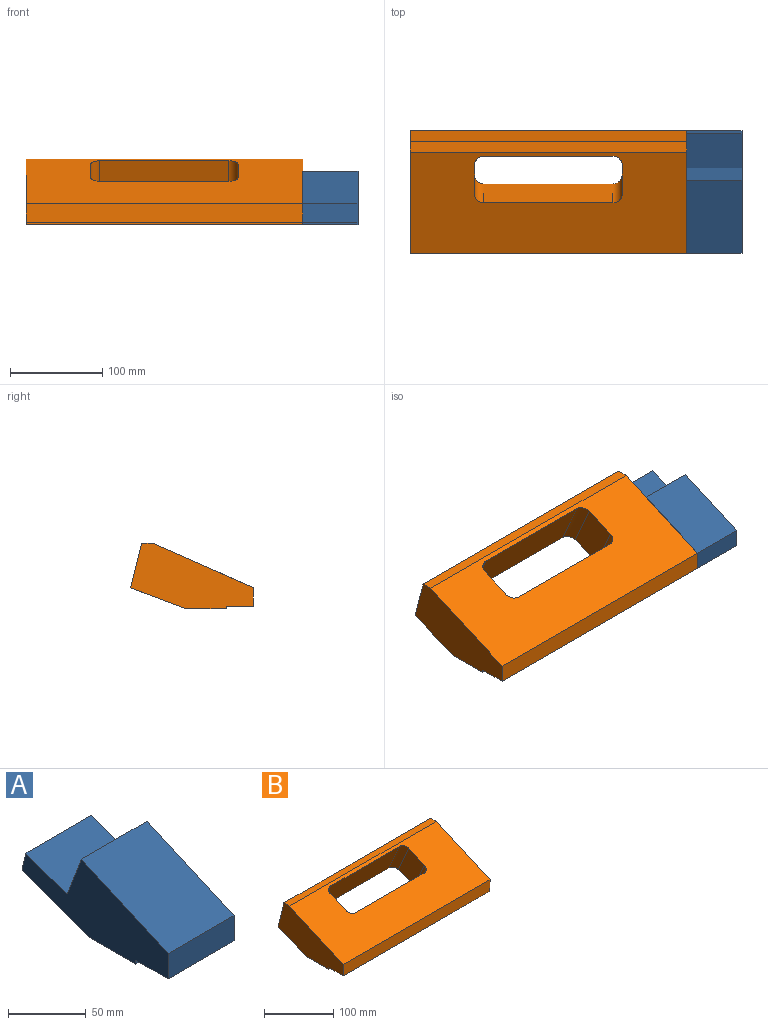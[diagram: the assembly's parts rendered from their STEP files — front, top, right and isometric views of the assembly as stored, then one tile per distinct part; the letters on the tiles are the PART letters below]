
ASSEMBLY  parts=2 mates=1
PART A: 11 faces, bbox 60x133.3x58 mm
  f0: plane 60x37.41mm, normal (0,-0.35,0.94), area 2400mm2, adj f1,f8,f9,f10
  f1: plane 60x34.59mm, normal (0,0.94,0.35), area 2219.1mm2, adj f0,f2,f9,f10
  f2: plane 79.17x60mm, normal (0,-0.4,0.91), area 5193.3mm2, adj f1,f3,f9,f10
  f3: plane 60x20mm, normal (0,-1,0), area 1200mm2, adj f2,f4,f9,f10
  f4: plane 60x29.5mm, normal (0,0,-1), area 1770mm2, adj f3,f5,f9,f10
  f5: plane 60x3mm, normal (0,-1,0), area 180mm2, adj f4,f6,f9,f10
  f6: plane 60x43mm, normal (0,0,-1), area 2580mm2, adj f5,f7,f9,f10
  f7: plane 60.79x60mm, normal (0,0.35,-0.94), area 3900mm2, adj f6,f8,f9,f10
  f8: plane 60x14.55mm, normal (0,0.97,0.24), area 900mm2, adj f0,f7,f9,f10
  f9: plane 133.29x57.99mm, normal (1,0,0), area 4201.1mm2, adj f0,f1,f2,f3,f4,f5,f6,f7
  f10: plane 133.29x57.99mm, normal (-1,0,0), area 4201.1mm2, adj f0,f1,f2,f3,f4,f5,f6,f7
PART B: 18 faces, bbox 300x133.3x71.5 mm
  f0: plane 300x109.76mm, normal (0,-0.4,0.91), area 27285.8mm2, adj f1,f7,f8,f9,f10,f11,f12,f13
  f1: plane 300x20mm, normal (0,-1,0), area 6000mm2, adj f0,f2,f8,f9
  f2: plane 300x29.5mm, normal (0,0,-1), area 8850mm2, adj f1,f3,f8,f9
  f3: plane 300x3mm, normal (0,-1,0), area 900mm2, adj f2,f4,f8,f9
  f4: plane 300x43mm, normal (0,0,-1), area 12900mm2, adj f3,f5,f8,f9
  f5: plane 300x60.79mm, normal (0,0.35,-0.94), area 10772.9mm2, adj f4,f6,f8,f9,f10,f11,f12,f13
  f6: plane 300x48.51mm, normal (0,0.97,0.24), area 15000mm2, adj f5,f7,f8,f9
  f7: plane 300x11.44mm, normal (0,0,1), area 3432.9mm2, adj f0,f6,f8,f9
  f8: plane 133.29x71.51mm, normal (1,0,0), area 5789.1mm2, adj f0,f1,f2,f3,f4,f5,f6,f7
  f9: plane 133.29x71.51mm, normal (-1,0,0), area 5789.1mm2, adj f0,f1,f2,f3,f4,f5,f6,f7
  f10: cylinder r=10mm len=50.74mm, axis (0,-0.4,0.91), area 796.5mm2, adj f0,f5,f11,f17
  f11: plane 140x46.2mm, normal (0,0.91,0.4), area 7071.5mm2, adj f0,f5,f10,f12
  f12: cylinder r=10mm len=50.74mm, axis (0,-0.4,0.91), area 796.5mm2, adj f0,f5,f11,f13
  f13: plane 60.85x53.43mm, normal (-1,0,0), area 1820.4mm2, adj f0,f5,f12,f14
  f14: cylinder r=10mm len=52.99mm, axis (0,-0.4,0.91), area 837.5mm2, adj f0,f5,f13,f15
  f15: plane 140x48.94mm, normal (0,-0.91,-0.4), area 7491.7mm2, adj f0,f5,f14,f16
  f16: cylinder r=10mm len=52.99mm, axis (0,-0.4,0.91), area 837.5mm2, adj f0,f5,f15,f17
  f17: plane 60.85x53.43mm, normal (1,0,0), area 1820.4mm2, adj f0,f5,f10,f16
PLACE A t=(128.92,-59.41,0.36)mm
PLACE B t=(-171.08,-59.41,0.36)mm
MATE parallel B.f8 <-> A.f10  axis (1,0,0) through (128.92,-59.41,-9.64)mm
